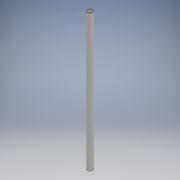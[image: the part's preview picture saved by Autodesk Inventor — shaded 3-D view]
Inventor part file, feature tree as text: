
AUTODESK INVENTOR PART (.ipt)
format: ipt  version: 2018.2 (Build 222227000, 227)  size: 92,160 bytes
history: native  units: mm
features: other x1, extrude x1, sketch x1
ambient origin geometry x8: Origin, YZ Plane, XZ Plane, XY Plane, X Axis, Y Axis, Z Axis, Center Point
bodies: Body1 (feature_tree)
feature tree (3):
  other  "ソリッド1"
  extrude  "押し出し1"  Depth=16.0mm
  sketch  "スケッチ1"
